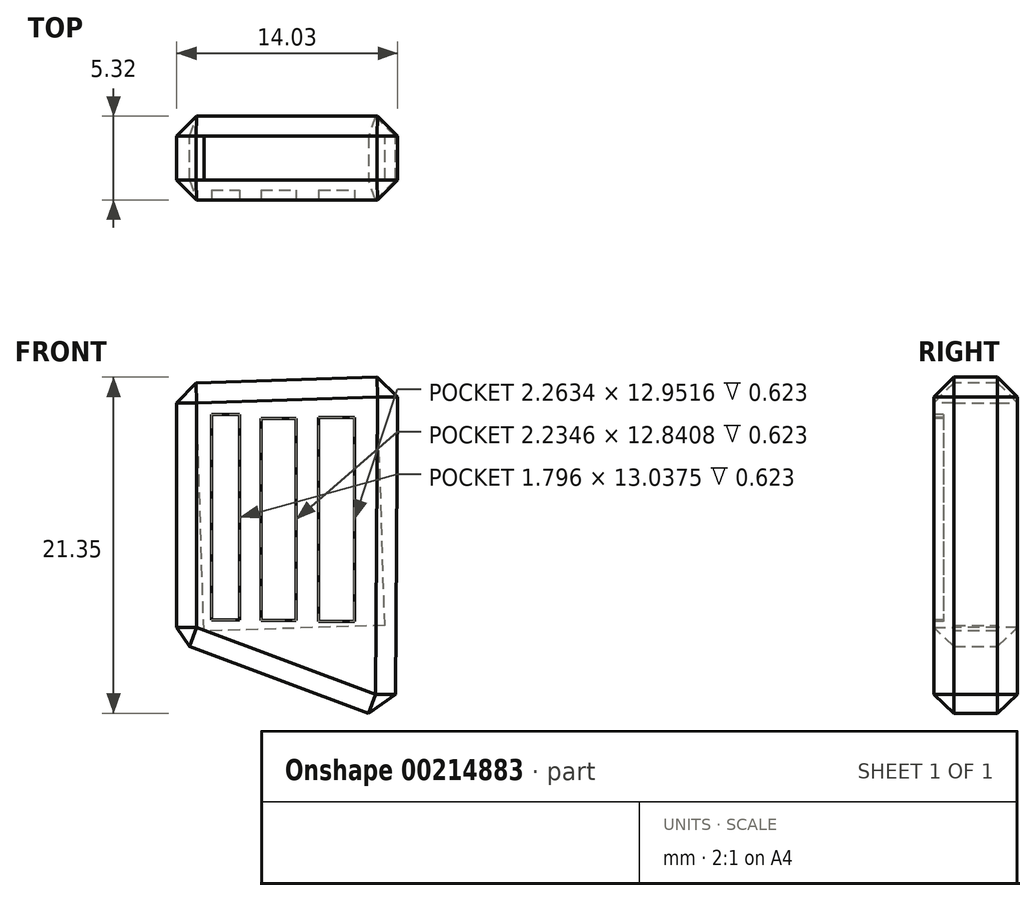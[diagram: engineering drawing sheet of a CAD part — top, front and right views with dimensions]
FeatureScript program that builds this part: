
annotation { "Feature Type Name" : "Feature", "Feature Type Description" : "" }
export const myFeature = defineFeature(function(context is Context, id is Id, definition is map)
    precondition{}
    {
        {
            var Q0;
            Q0=qCreatedBy(makeId("Front.planeOp"),FACE);
            var sketch = newSketch(context, id + "F4", { "sketchPlane" : qUnion([Q0])});
            skLineSegment(sketch, "E0", {"start": v(-13.89, 0) * mm, "end": v(-13.89, -16.38) * mm});
            skLineSegment(sketch, "E1", {"start": v(-13.89, -16.38) * mm, "end": v(0, -21.59) * mm});
            skLineSegment(sketch, "E2", {"start": v(0, -21.59) * mm, "end": v(0.15, 0.44) * mm});
            skLineSegment(sketch, "E3", {"start": v(0.15, 0.44) * mm, "end": v(-13.89, 0) * mm});
            skSolve(sketch);
        }
        {
            var Q0;
            Q0 = qSketchRegion(id + "F4", true);
            extrude(context, id + "F0", {"entities" : qUnion([Q0]), "depth" : 5.32 * mm});
        }
        {
            var Q0;
            Q0=makeQuery(id+"F0.opExtrude","CAP_EDGE",EDGE,{"disambiguationData":[OSD([sQuery(id+"F4.wireOp",EDGE,"E0")])],"isStart":false});
            var Q1;
            Q1=makeQuery(id+"F0.opExtrude","CAP_EDGE",EDGE,{"disambiguationData":[OSD([sQuery(id+"F4.wireOp",EDGE,"E3")])],"isStart":false});
            var Q2;
            Q2=makeQuery(id+"F0.opExtrude","CAP_EDGE",EDGE,{"disambiguationData":[OSD([sQuery(id+"F4.wireOp",EDGE,"E1")])],"isStart":false});
            var Q3;
            Q3=makeQuery(id+"F0.opExtrude","CAP_EDGE",EDGE,{"disambiguationData":[OSD([sQuery(id+"F4.wireOp",EDGE,"E2")])],"isStart":false});
            var Q4;
            Q4=makeQuery(id+"F0.opExtrude","SWEPT_EDGE",EDGE,{"disambiguationData":[OSD([sQuery(id+"F4.wireOp",EDGE,"E1"),sQuery(id+"F4.wireOp",EDGE,"E2")])]});
            var Q5;
            Q5=makeQuery(id+"F0.opExtrude","SWEPT_EDGE",EDGE,{"disambiguationData":[OSD([sQuery(id+"F4.wireOp",EDGE,"E0"),sQuery(id+"F4.wireOp",EDGE,"E1")])]});
            var Q6;
            Q6=makeQuery(id+"F0.opExtrude","CAP_EDGE",EDGE,{"disambiguationData":[OSD([sQuery(id+"F4.wireOp",EDGE,"E1")])],"isStart":true});
            var Q7;
            Q7=makeQuery(id+"F0.opExtrude","CAP_EDGE",EDGE,{"disambiguationData":[OSD([sQuery(id+"F4.wireOp",EDGE,"E0")])],"isStart":true});
            var Q8;
            Q8=makeQuery(id+"F0.opExtrude","SWEPT_EDGE",EDGE,{"disambiguationData":[OSD([sQuery(id+"F4.wireOp",EDGE,"E0"),sQuery(id+"F4.wireOp",EDGE,"E3")])]});
            var Q9;
            Q9=makeQuery(id+"F0.opExtrude","CAP_EDGE",EDGE,{"disambiguationData":[OSD([sQuery(id+"F4.wireOp",EDGE,"E3")])],"isStart":true});
            var Q10;
            Q10=makeQuery(id+"F0.opExtrude","SWEPT_EDGE",EDGE,{"disambiguationData":[OSD([sQuery(id+"F4.wireOp",EDGE,"E2"),sQuery(id+"F4.wireOp",EDGE,"E3")])]});
            var Q11;
            Q11=makeQuery(id+"F0.opExtrude","CAP_EDGE",EDGE,{"disambiguationData":[OSD([sQuery(id+"F4.wireOp",EDGE,"E2")])],"isStart":true});
            chamfer(context, id + "F1", {"entities" : qUnion([Q0, Q1, Q2, Q3, Q4, Q5, Q6, Q7, Q8, Q9, Q10, Q11]), "width" : 1.27 * mm, "tangentPropagation" : true});
        }
        {
            var Q0;
            Q0=makeQuery(id+"F0.opExtrude","SWEPT_FACE",FACE,{"disambiguationData":[OSD([sQuery(id+"F4.wireOp",EDGE,"E3")])]});
            extrude(context, id + "F5", {"entities" : qUnion([Q0]), "operationType" : NewBodyOperationType.REMOVE, "oppositeDirection" : true, "depth" : 15.78 * mm});
        }
        {
            var Q0;
            Q0=makeQuery(id+"F0.opExtrude","CAP_FACE",FACE,{"disambiguationData":[OSD([sQuery(id+"F4.wireOp",EDGE,"E0"),sQuery(id+"F4.wireOp",EDGE,"E1"),sQuery(id+"F4.wireOp",EDGE,"E2"),sQuery(id+"F4.wireOp",EDGE,"E3")])],"isStart":false});
            var sketch = newSketch(context, id + "F2", { "sketchPlane" : qUnion([Q0])});
            skLineSegment(sketch, "E4.bottom", {"start": v(-11.68, -1.98) * mm, "end": v(-9.88, -1.98) * mm});
            skLineSegment(sketch, "E4.top", {"start": v(-11.68, -15.02) * mm, "end": v(-9.88, -15.02) * mm});
            skLineSegment(sketch, "E4.left", {"start": v(-11.68, -1.98) * mm, "end": v(-11.68, -15.02) * mm});
            skLineSegment(sketch, "E4.right", {"start": v(-9.88, -1.98) * mm, "end": v(-9.88, -15.02) * mm});
            skLineSegment(sketch, "E5.bottom", {"start": v(-8.54, -2.22) * mm, "end": v(-6.3, -2.22) * mm});
            skLineSegment(sketch, "E5.top", {"start": v(-8.54, -15.06) * mm, "end": v(-6.3, -15.06) * mm});
            skLineSegment(sketch, "E5.left", {"start": v(-8.54, -2.22) * mm, "end": v(-8.54, -15.06) * mm});
            skLineSegment(sketch, "E5.right", {"start": v(-6.3, -2.22) * mm, "end": v(-6.3, -15.06) * mm});
            skLineSegment(sketch, "E6.bottom", {"start": v(-4.87, -2.15) * mm, "end": v(-2.6, -2.15) * mm});
            skLineSegment(sketch, "E6.top", {"start": v(-4.87, -15.1) * mm, "end": v(-2.6, -15.1) * mm});
            skLineSegment(sketch, "E6.left", {"start": v(-4.87, -2.15) * mm, "end": v(-4.87, -15.1) * mm});
            skLineSegment(sketch, "E6.right", {"start": v(-2.6, -2.15) * mm, "end": v(-2.6, -15.1) * mm});
            skSolve(sketch);
        }
        {
            var Q0;
            Q0 = qSketchRegion(id + "F2", true);
            extrude(context, id + "F3", {"entities" : qUnion([Q0]), "operationType" : NewBodyOperationType.REMOVE, "oppositeDirection" : true, "depth" : 0.62 * mm});
        }
    });
